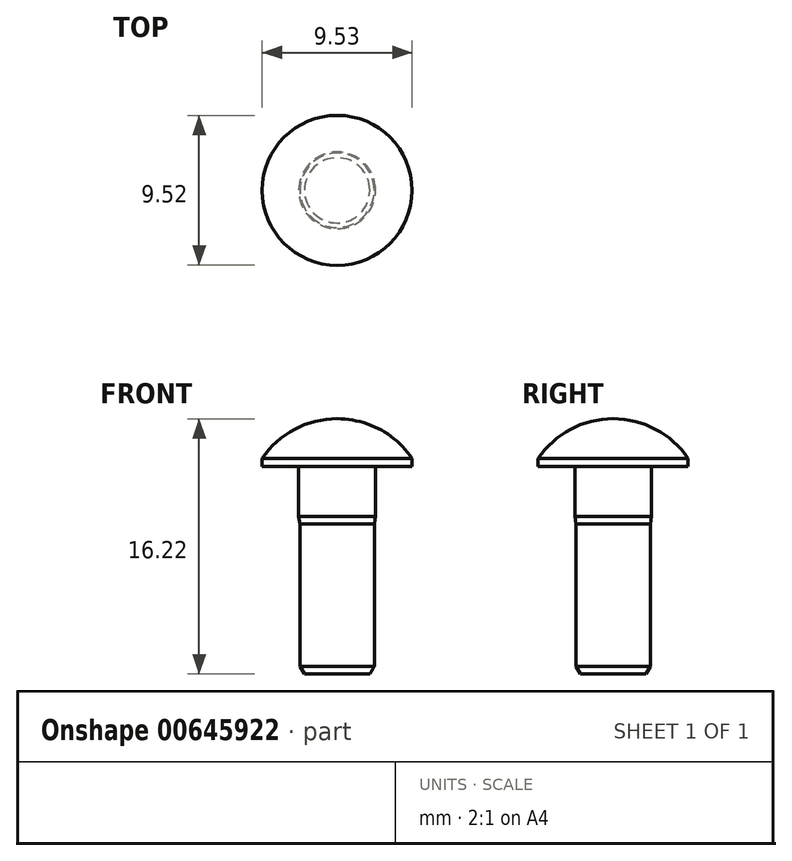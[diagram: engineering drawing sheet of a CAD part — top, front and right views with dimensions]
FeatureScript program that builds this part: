
annotation { "Feature Type Name" : "Feature", "Feature Type Description" : "" }
export const myFeature = defineFeature(function(context is Context, id is Id, definition is map)
    precondition{}
    {
        {
            var Q0;
            Q0=qCreatedBy(makeId("Front.planeOp"),FACE);
            var sketch = newSketch(context, id + "F0", { "sketchPlane" : qUnion([Q0])});
            skLineSegment(sketch, "E0", {"start": v(0, 0) * mm, "end": v(0, 0.5) * mm});
            skArc(sketch, "E1", {"start": v(4.76, 3.02) * mm, "mid": v(2.07, 2.35) * mm, "end": v(0, 0.5) * mm});
            skLineSegment(sketch, "E2", {"start": v(4.76, 3.02) * mm, "end": v(7.96, 3.02) * mm, "construction": true});
            skLineSegment(sketch, "E3", {"start": v(0, 0) * mm, "end": v(2.32, 0) * mm});
            skLineSegment(sketch, "E4", {"start": v(2.32, 0) * mm, "end": v(2.32, -3.18) * mm});
            skLineSegment(sketch, "E5", {"start": v(2.32, -3.18) * mm, "end": v(2.4, -3.68) * mm});
            skLineSegment(sketch, "E6", {"start": v(2.4, -3.68) * mm, "end": v(2.4, -12.7) * mm});
            skLineSegment(sketch, "E7", {"start": v(2.4, -12.7) * mm, "end": v(2.69, -13.2) * mm});
            skLineSegment(sketch, "E8", {"start": v(2.69, -13.2) * mm, "end": v(4.76, -13.2) * mm});
            skLineSegment(sketch, "E9", {"start": v(4.76, 3.02) * mm, "end": v(4.76, 0) * mm});
            skLineSegment(sketch, "E10", {"start": v(4.76, 0) * mm, "end": v(4.76, -13.2) * mm});
            skSolve(sketch);
        }
        {
            var Q0;
            Q0 = qSketchRegion(id + "F0", true);
            var Q1;
            Q1=sQuery(id+"F0.wireOp",EDGE,"E10");
            revolve(context, id + "F1", {"entities" : qUnion([Q0]), "axis" : qUnion([Q1]), "revolveType" : RevolveType.FULL});
        }
    });
